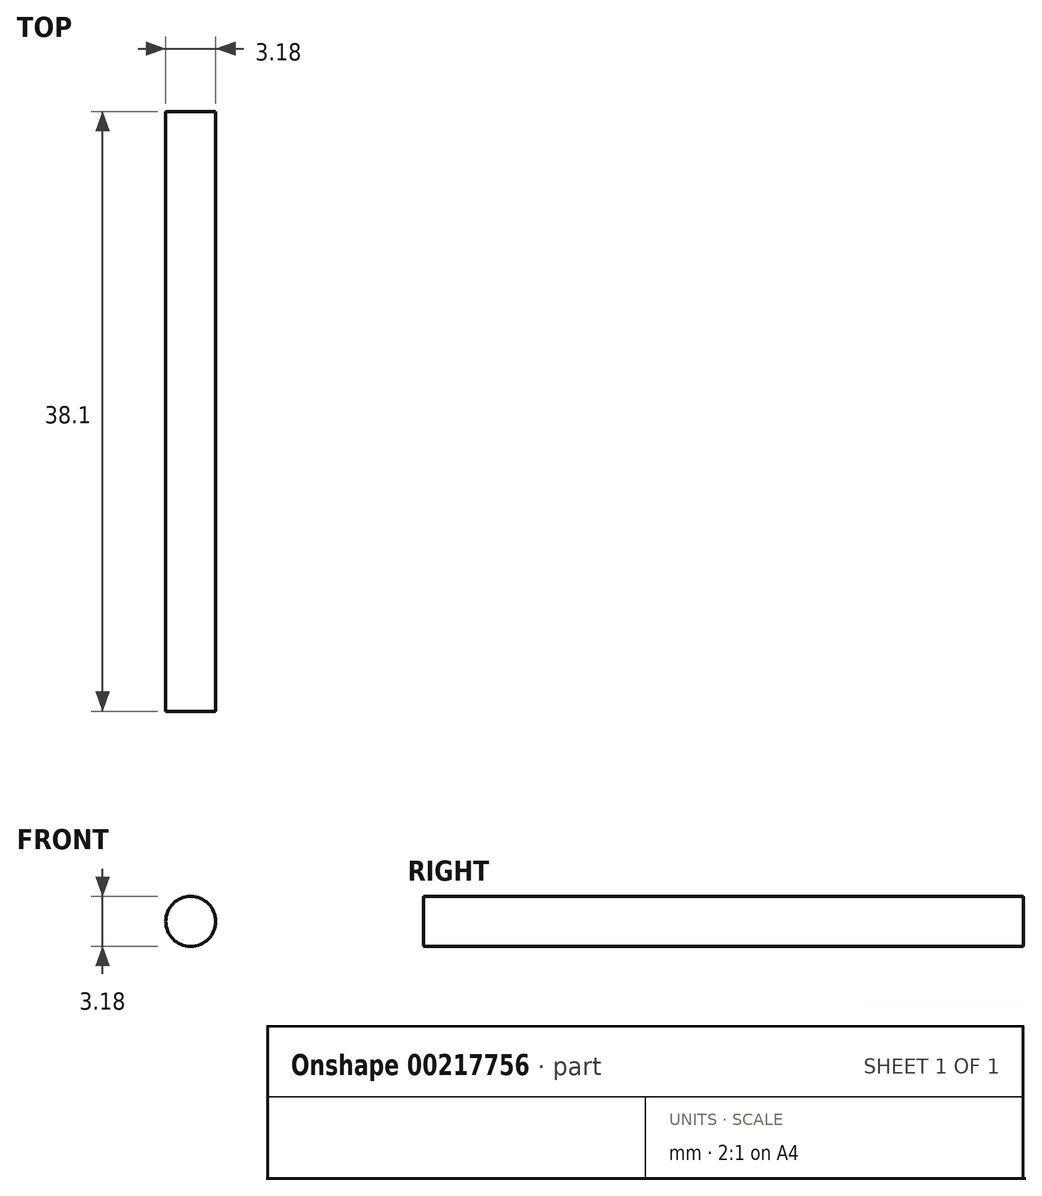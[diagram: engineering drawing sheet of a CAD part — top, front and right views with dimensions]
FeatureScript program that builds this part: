
annotation { "Feature Type Name" : "Feature", "Feature Type Description" : "" }
export const myFeature = defineFeature(function(context is Context, id is Id, definition is map)
    precondition{}
    {
        {
            var Q0;
            Q0=qCreatedBy(makeId("Front.planeOp"),FACE);
            var sketch = newSketch(context, id + "F0", { "sketchPlane" : qUnion([Q0])});
            skCircle(sketch, "E0", {"center": v(0, 0) * mm, "radius": 1.59 * mm});
            skSolve(sketch);
        }
        {
            var Q0;
            Q0 = qSketchRegion(id + "F0", true);
            extrude(context, id + "F1", {"entities" : qUnion([Q0]), "depth" : 38.1 * mm});
        }
    });
